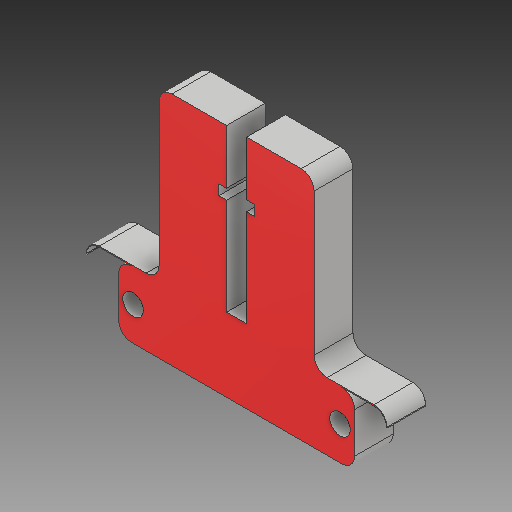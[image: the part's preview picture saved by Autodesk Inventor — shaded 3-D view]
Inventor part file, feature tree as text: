
AUTODESK INVENTOR PART (.ipt)
format: ipt  version: 2018 (Build 220112000, 112)  size: 184,832 bytes
history: native  units: mm
features: sketch x6, other x3
ambient origin geometry x8: Origin, YZ Plane, XZ Plane, XY Plane, X Axis, Y Axis, Z Axis, Center Point
bodies: Solid1 (feature_tree)
feature tree (9):
  other  "Hotend Slide Part 1.ipt"
  other  "Solid1::Hotend Slide Part 1.ipt"
  other  "TaggingFeature1"
  sketch  "Sketch1"  dims[d0=10.0mm]
  sketch  "Sketch2"
  sketch  "Sketch3"
  sketch  "Sketch4"
  sketch  "Sketch5"
  sketch  "Sketch6"
